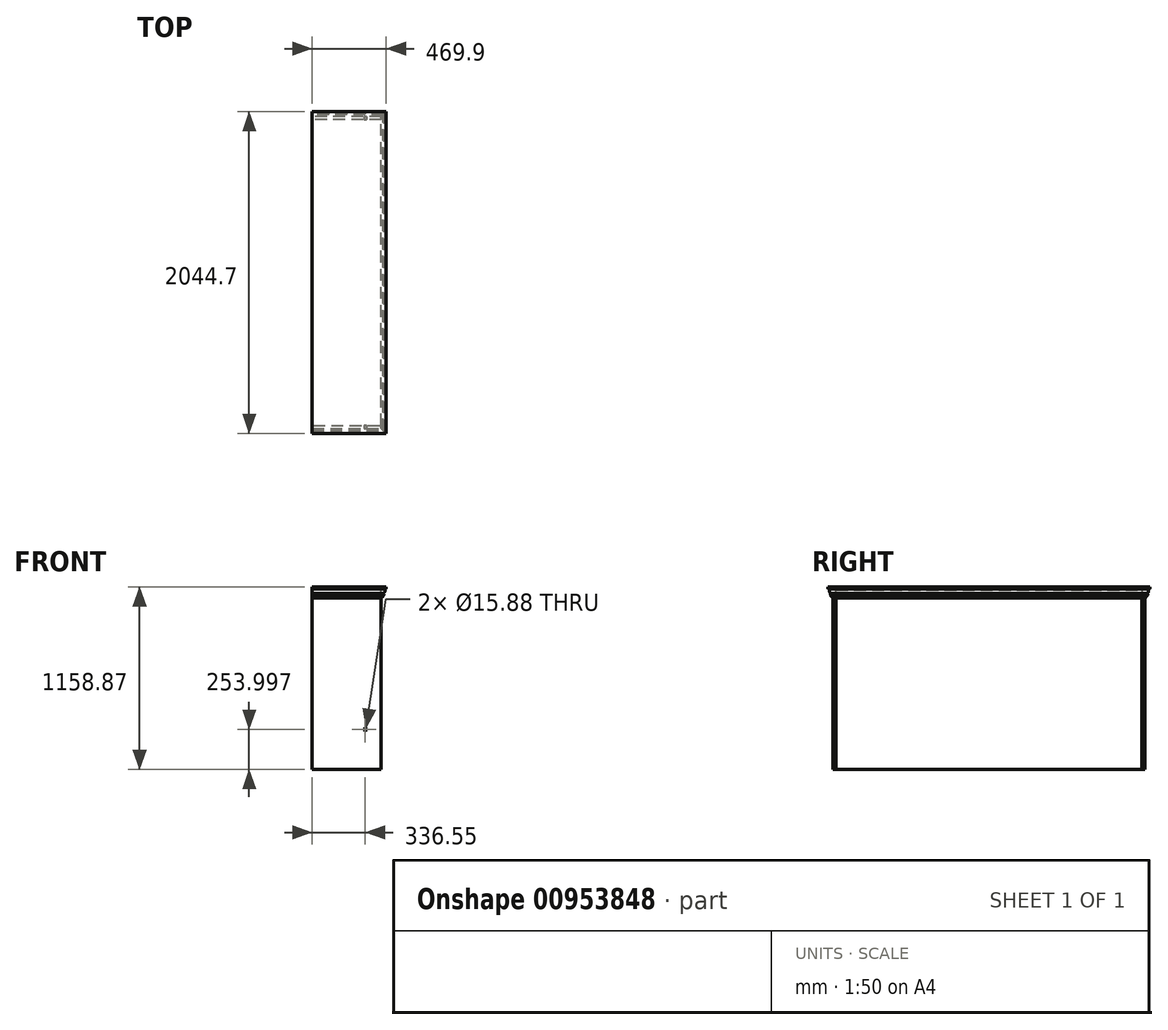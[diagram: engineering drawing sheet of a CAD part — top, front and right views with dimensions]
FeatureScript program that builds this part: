
annotation { "Feature Type Name" : "Feature", "Feature Type Description" : "" }
export const myFeature = defineFeature(function(context is Context, id is Id, definition is map)
    precondition{}
    {
        {
            var Q0;
            Q0=qCreatedBy(makeId("Front.planeOp"),FACE);
            var sketch = newSketch(context, id + "F0", { "sketchPlane" : qUnion([Q0])});
            skLineSegment(sketch, "E0.bottom", {"start": v(-215.9, -569.91) * mm, "end": v(215.9, -569.91) * mm});
            skLineSegment(sketch, "E0.top", {"start": v(-215.9, 569.91) * mm, "end": v(215.9, 569.91) * mm});
            skLineSegment(sketch, "E0.left", {"start": v(-215.9, -569.91) * mm, "end": v(-215.9, 569.91) * mm});
            skLineSegment(sketch, "E0.right", {"start": v(215.9, -569.91) * mm, "end": v(215.9, 569.91) * mm});
            skPoint(sketch, "E0.middle", {"position": v(0, 0) * mm});
            skSolve(sketch);
        }
        {
            var Q0;
            Q0=makeQuery(id+"F0.imprint","IMPRINT",FACE,{"disambiguationData":[TD([[makeQuery(id+"F0.imprint","IMPRINT",EDGE,{"derivedFrom":sQuery(id+"F0.wireOp",EDGE,"E0.bottom")}),1.0]])]});
            extrude(context, id + "F1", {"entities" : qUnion([Q0]), "depth" : 19.05 * mm, "offsetDistance" : 25.4 * mm});
        }
        {
            var Q0;
            Q0=makeQuery(id+"F1.opExtrude","SWEPT_FACE",FACE,{"disambiguationData":[OSD([sQuery(id+"F0.wireOp",EDGE,"E0.top")])]});
            var sketch = newSketch(context, id + "F2", { "sketchPlane" : qUnion([Q0])});
            skLineSegment(sketch, "E1.bottom", {"start": v(-215.9, -19.05) * mm, "end": v(215.9, -19.05) * mm});
            skLineSegment(sketch, "E1.top", {"start": v(-215.9, 1962.15) * mm, "end": v(215.9, 1962.15) * mm});
            skLineSegment(sketch, "E1.left", {"start": v(-215.9, -19.05) * mm, "end": v(-215.9, 1962.15) * mm});
            skLineSegment(sketch, "E1.right", {"start": v(215.9, -19.05) * mm, "end": v(215.9, 1962.15) * mm});
            skSolve(sketch);
        }
        {
            var Q0;
            Q0 = qSketchRegion(id + "F2", true);
            extrude(context, id + "F3", {"entities" : qUnion([Q0]), "operationType" : NewBodyOperationType.ADD, "depth" : 19.05 * mm, "offsetDistance" : 25.4 * mm});
        }
        {
            var Q0;
            Q0=makeQuery(id+"F3.opExtrude","SWEPT_FACE",FACE,{"disambiguationData":[OSD([sQuery(id+"F2.wireOp",EDGE,"E1.top")])]});
            var sketch = newSketch(context, id + "F4", { "sketchPlane" : qUnion([Q0])});
            skLineSegment(sketch, "E2.bottom", {"start": v(-215.9, 588.96) * mm, "end": v(215.9, 588.96) * mm});
            skLineSegment(sketch, "E2.top", {"start": v(-215.9, -569.91) * mm, "end": v(215.9, -569.91) * mm});
            skLineSegment(sketch, "E2.left", {"start": v(-215.9, 588.96) * mm, "end": v(-215.9, -569.91) * mm});
            skLineSegment(sketch, "E2.right", {"start": v(215.9, 588.96) * mm, "end": v(215.9, -569.91) * mm});
            skSolve(sketch);
        }
        {
            var Q0;
            Q0 = qSketchRegion(id + "F4", true);
            extrude(context, id + "F5", {"entities" : qUnion([Q0]), "operationType" : NewBodyOperationType.ADD, "oppositeDirection" : true, "depth" : 19.05 * mm, "offsetDistance" : 25.4 * mm});
        }
        {
            var Q0;
            Q0=makeQuery(id+"F5.boolean.opBoolean","MERGE",FACE,{"derivedFrom":[makeQuery(id+"F3.boolean.opBoolean","MERGE",FACE,{"derivedFrom":[makeQuery(id+"F1.opExtrude","SWEPT_FACE",FACE,{"disambiguationData":[OSD([sQuery(id+"F0.wireOp",EDGE,"E0.left")])]}),makeQuery(id+"F3.opExtrude","SWEPT_FACE",FACE,{"disambiguationData":[OSD([sQuery(id+"F2.wireOp",EDGE,"E1.left")])]})]}),makeQuery(id+"F5.opExtrude","SWEPT_FACE",FACE,{"disambiguationData":[OSD([sQuery(id+"F4.wireOp",EDGE,"E2.right")])]})]});
            var sketch = newSketch(context, id + "F6", { "sketchPlane" : qUnion([Q0])});
            skLineSegment(sketch, "E3.bottom", {"start": v(-1962.15, 588.96) * mm, "end": v(19.05, 588.96) * mm});
            skLineSegment(sketch, "E3.top", {"start": v(-1962.15, -569.91) * mm, "end": v(19.05, -569.91) * mm});
            skLineSegment(sketch, "E3.left", {"start": v(-1962.15, 588.96) * mm, "end": v(-1962.15, -569.91) * mm});
            skLineSegment(sketch, "E3.right", {"start": v(19.05, 588.96) * mm, "end": v(19.05, -569.91) * mm});
            skSolve(sketch);
        }
        {
            var Q0;
            Q0 = qSketchRegion(id + "F6", true);
            extrude(context, id + "F7", {"entities" : qUnion([Q0]), "operationType" : NewBodyOperationType.ADD, "depth" : 6.35 * mm, "offsetDistance" : 25.4 * mm});
        }
        {
            var Q0;
            Q0=makeQuery(id+"F7.boolean.opBoolean","MERGE",FACE,{"derivedFrom":[makeQuery(id+"F3.boolean.opBoolean","MERGE",FACE,{"derivedFrom":[makeQuery(id+"F1.opExtrude","CAP_FACE",FACE,{"disambiguationData":[OSD([sQuery(id+"F0.wireOp",EDGE,"E0.bottom"),sQuery(id+"F0.wireOp",EDGE,"E0.top"),sQuery(id+"F0.wireOp",EDGE,"E0.left"),sQuery(id+"F0.wireOp",EDGE,"E0.right")])],"isStart":false}),makeQuery(id+"F3.opExtrude","SWEPT_FACE",FACE,{"disambiguationData":[OSD([sQuery(id+"F2.wireOp",EDGE,"E1.bottom")])]})]}),makeQuery(id+"F7.opExtrude","SWEPT_FACE",FACE,{"disambiguationData":[OSD([sQuery(id+"F6.wireOp",EDGE,"E3.right")])]})]});
            var sketch = newSketch(context, id + "F8", { "sketchPlane" : qUnion([Q0])});
            skCircle(sketch, "E4", {"center": v(114.3, -315.91) * mm, "radius": 7.94 * mm});
            skSolve(sketch);
        }
        {
            var Q0;
            Q0 = qSketchRegion(id + "F8", true);
            extrude(context, id + "F9", {"entities" : qUnion([Q0]), "operationType" : NewBodyOperationType.REMOVE, "endBound" : BoundingType.THROUGH_ALL, "oppositeDirection" : true, "depth" : 25.4 * mm, "offsetDistance" : 25.4 * mm});
        }
        {
            var Q0;
            Q0=makeQuery(id+"F7.opExtrude","CAP_FACE",FACE,{"disambiguationData":[OSD([sQuery(id+"F6.wireOp",EDGE,"E3.bottom"),sQuery(id+"F6.wireOp",EDGE,"E3.top"),sQuery(id+"F6.wireOp",EDGE,"E3.left"),sQuery(id+"F6.wireOp",EDGE,"E3.right")])],"isStart":false});
            var sketch = newSketch(context, id + "F10", { "sketchPlane" : qUnion([Q0])});
            skLineSegment(sketch, "E5", {"start": v(19.05, 588.96) * mm, "end": v(50.8, 588.96) * mm});
            skLineSegment(sketch, "E6", {"start": v(19.05, 588.96) * mm, "end": v(19.05, 519.11) * mm});
            skLineSegment(sketch, "E7", {"start": v(50.8, 588.96) * mm, "end": v(50.8, 576.26) * mm});
            skFitSpline(sketch, "E8", {"points": [v(50.8, 576.26) * mm, v(41.9, 568.43) * mm, v(41, 558.06) * mm, v(31.75, 549.08) * mm], "startDerivative": vector(-56.77, -4.03) * mm, "endDerivative": vector(-38.32, -18.33) * mm});
            skLineSegment(sketch, "E9", {"start": v(31.75, 549.08) * mm, "end": v(31.75, 544) * mm});
            skArc(sketch, "E10", {"start": v(31.75, 536.56) * mm, "mid": v(36.38, 540.28) * mm, "end": v(31.75, 544) * mm});
            skLineSegment(sketch, "E11", {"start": v(31.75, 536.56) * mm, "end": v(31.75, 531.81) * mm});
            skFitSpline(sketch, "E12", {"points": [v(31.75, 531.81) * mm, v(27.13, 526.7) * mm, v(24.22, 523.36) * mm, v(19.05, 519.11) * mm], "startDerivative": vector(-0.07, -35.6) * mm, "endDerivative": vector(-38.4, -2.1) * mm});
            skSolve(sketch);
        }
        {
            var Q0;
            Q0 = qSketchRegion(id + "F10", true);
            var Q1;
            Q1=makeQuery(id+"F7.boolean.opBoolean","MERGE",EDGE,{"derivedFrom":[makeQuery(id+"F3.opExtrude","CAP_EDGE",EDGE,{"disambiguationData":[OSD([sQuery(id+"F2.wireOp",EDGE,"E1.bottom")])],"isStart":false}),makeQuery(id+"F7.opExtrude","SWEPT_EDGE",EDGE,{"disambiguationData":[OSD([sQuery(id+"F6.wireOp",EDGE,"E3.bottom"),sQuery(id+"F6.wireOp",EDGE,"E3.right")])]})]});
            var Q2;
            Q2=makeQuery(id+"F3.opExtrude","CAP_EDGE",EDGE,{"disambiguationData":[OSD([sQuery(id+"F2.wireOp",EDGE,"E1.right")])],"isStart":false});
            var Q3;
            Q3=makeQuery(id+"F7.boolean.opBoolean","MERGE",EDGE,{"derivedFrom":[makeQuery(id+"F3.opExtrude","CAP_EDGE",EDGE,{"disambiguationData":[OSD([sQuery(id+"F2.wireOp",EDGE,"E1.top")])],"isStart":false}),makeQuery(id+"F7.opExtrude","SWEPT_EDGE",EDGE,{"disambiguationData":[OSD([sQuery(id+"F6.wireOp",EDGE,"E3.bottom"),sQuery(id+"F6.wireOp",EDGE,"E3.left")])]})]});
            sweep(context, id + "F11", {"operationType" : NewBodyOperationType.ADD, "profiles" : qUnion([Q0]), "path" : qUnion([Q1, Q2, Q3])});
        }
    });
